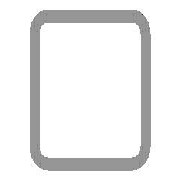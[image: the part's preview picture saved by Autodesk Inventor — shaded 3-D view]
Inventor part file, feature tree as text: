
AUTODESK INVENTOR PART (.ipt)
format: ipt  version: 2025 (Build 290162010, 162A)  size: 132,608 bytes
history: native  units: mm (DEFAULTED — no unit token found)
features: other x4, sketch x1, plane x1
ambient origin geometry x8: Origin, YZ Plane, XZ Plane, XY Plane, X Axis, Y Axis, Z Axis, Center Point
bodies: Solid1 (feature_tree), Body (feature_tree)
feature tree (6):
  parser-record x1  (decoder bookkeeping rows leaked as tree rows — omitted from the tree; the rows remain in map.json)
  other  "Driven Length"
  other  "Start Plane"
  other  "End Plane"
  sketch  "Sketch3"  dims[d3=550.0mm d4=0.0mm d7=8.0mm d9=100.0mm d11=100.0mm d12=4.0mm d13=100.0mm d14=650.0mm d15=50.0mm d16=50.0mm d17=90.0deg d18=550.0mm]
  plane  "Work Plane3"
